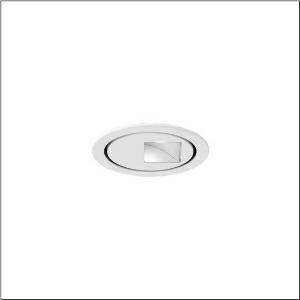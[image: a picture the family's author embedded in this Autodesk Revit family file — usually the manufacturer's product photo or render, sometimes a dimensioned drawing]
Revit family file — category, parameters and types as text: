
# Revit family: lunis_11_micro_round_51dj11b71wm21
name_source: partatom
category: Lighting Fixtures
units: mm (PartAtom-declared; Revit-internal decimal feet)

## family parameters
Cut with Voids When Loaded = No
Host = Face
Light Source = No
Part Type = Normal
Room Calculation Point = No
Round Connector Dimension = Use Diameter
Shared = No

## types (1)
- Lunis 11 micro round (1 x LED 3000K / CRI = 90 (unbekannt), 1100 lm, 3000K)
    Apparent Load = 20 VA
    CIE Flux Codes = 42 75 96 100 100
    Color Rendering = 90
    Color Temperature = 3000K
    Default Elevation = 1800 mm
    Description = Lunis 11 micro round, downlight, light control with wallwasher, of highly reflective aluminium, highly specular, light emission: direct distribution, LED rated luminous flux: 1.100lm, light colour: 930, with terminal, 3-pole, mains connection: 220..230V, AC, 50/60Hz, LED module, of aluminium, highly specular, white, diameter: 114mm, clamping range: 1..40mm, recessing ring, of plastic, traffic white (RAL 9016), protection rating (complete): IP20, insulation class (complete): insulation class II (safety insulation), certification: CE, permissible ambient temperature for indoor applications: 0..+35°C, packaging unit: 1 piece
    Height = 0 mm  [stored 0 ft]
    Lamp = 1 x LED 3000K / CRI >= 90 (unbekannt)
    Lamp Light Flux = 1100 lm
    Lamp count = 1
    Length = 114 mm
    Luminous efficacy = 56 lm/W
    Manufacturer = Siteco
    ModVariant = No
    Model = 51DJ11B71WM21
    Mounting Place = Ceiling
    Mounting Type = Recessed
    Number of Poles = 1
    OnlyDefault = Yes
    Power Factor = 1
    Product Name = Lunis 11 micro round
    Product group = downlight
    ProductGroupID = 400
    Protection Class = Protection class II
    Protection Degree = IP 20
    RLX_Detail_Level = 1
    RLX_Emergency_Light_Flux = 0 lm
    RLX_Emergency_Type = 0
    RLX_Emergency_Type_DB = No
    RlxData = <blob elided: 40313 chars, md5=3dbedc7c>
    Socket = socket
    Standby Power = 0 W
    System Light Flux = 1100 lm
    System Power = 20 W
    Type Comments = Product without accessories
    Type Image = l_1004773.jpg
    URL = http://relux.com
    VarID = ---
    Voltage = 0 V
    Weight = 0.00 kg
    Width = 114 mm

note: [stored X ft] marks values corroborated as IEEE doubles in the binary element streams (Revit-internal decimal feet)

## geometry (parser evidence)
native form markers: Blend x4, Sweep x10
no freeform markers — native parametric forms only
